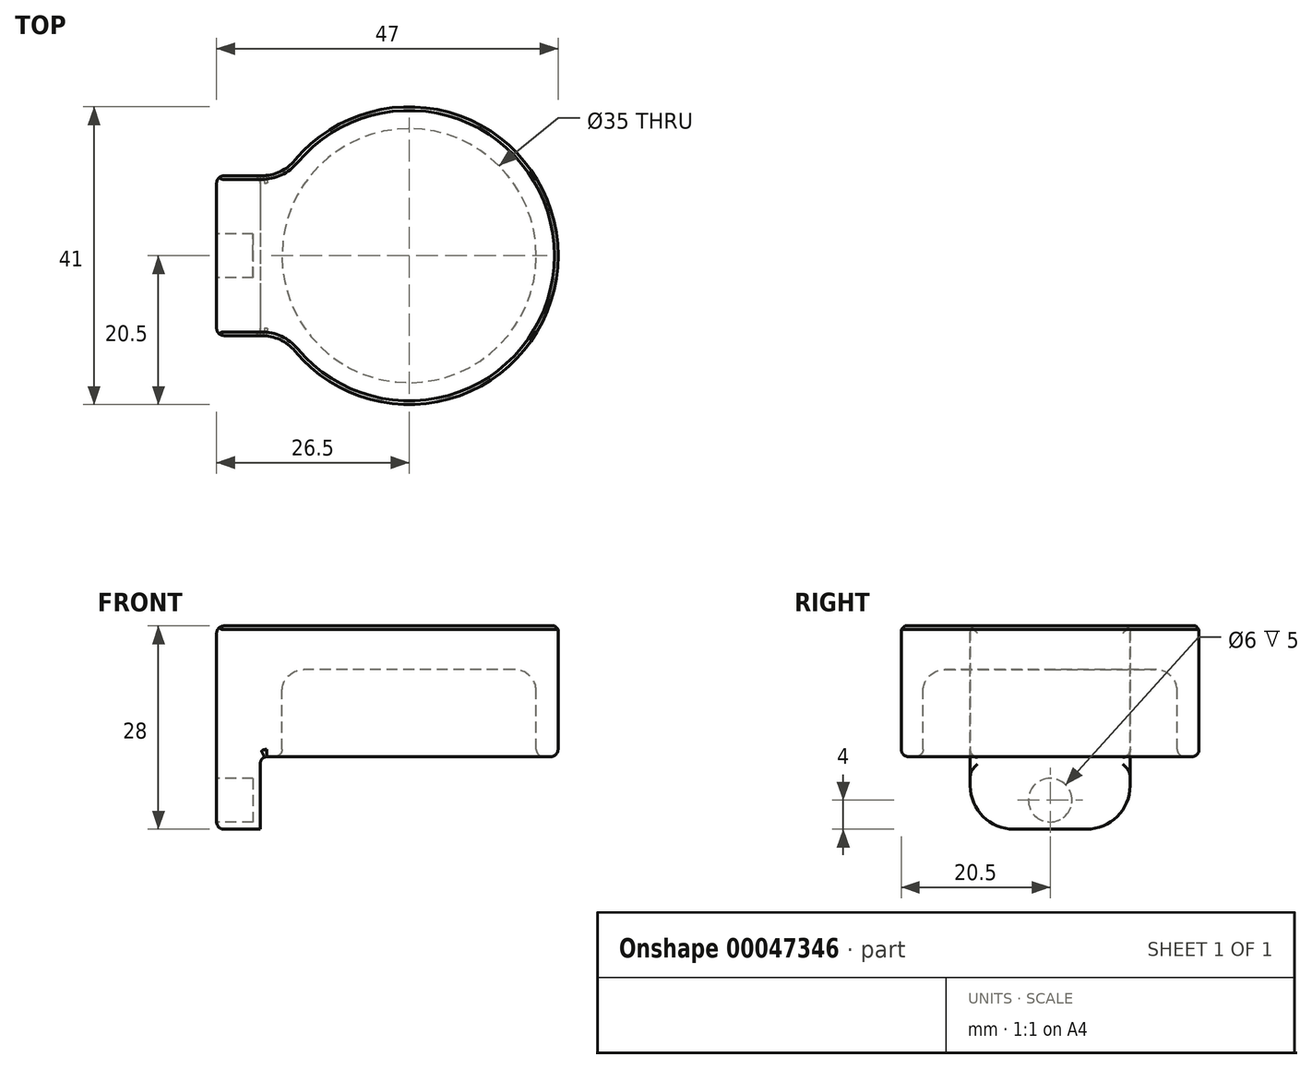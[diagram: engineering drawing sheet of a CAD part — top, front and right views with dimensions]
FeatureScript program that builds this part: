
annotation { "Feature Type Name" : "Feature", "Feature Type Description" : "" }
export const myFeature = defineFeature(function(context is Context, id is Id, definition is map)
    precondition{}
    {
        {
            var Q0;
            Q0=qCreatedBy(makeId("Top.planeOp"),FACE);
            var sketch = newSketch(context, id + "F0", { "sketchPlane" : qUnion([Q0])});
            skCircle(sketch, "E0", {"center": v(0, 0) * mm, "radius": 17.5 * mm});
            skArc(sketch, "E1", {"start": v(-17.3, -11) * mm, "mid": v(20.5, 0) * mm, "end": v(-17.3, 11) * mm});
            skLineSegment(sketch, "E2", {"start": v(-17.3, 11) * mm, "end": v(-26.5, 11) * mm});
            skLineSegment(sketch, "E3", {"start": v(-26.5, 11) * mm, "end": v(-26.5, -11) * mm});
            skLineSegment(sketch, "E4", {"start": v(-26.5, -11) * mm, "end": v(-17.3, -11) * mm});
            skLineSegment(sketch, "E5", {"start": v(0, 0) * mm, "end": v(-26.5, 0) * mm, "construction": true});
            skSolve(sketch);
        }
        {
            var Q0;
            Q0=makeQuery(id+"F0.imprint","IMPRINT",FACE,{"disambiguationData":[TD([[makeQuery(id+"F0.imprint","IMPRINT",EDGE,{"derivedFrom":sQuery(id+"F0.wireOp",EDGE,"E0")}),1.0]])]});
            extrude(context, id + "F1", {"entities" : qUnion([Q0]), "oppositeDirection" : true, "depth" : 6 * mm});
        }
        {
            var Q0;
            Q0=makeQuery(id+"F0.imprint","IMPRINT",FACE,{"disambiguationData":[TD([[makeQuery(id+"F0.imprint","IMPRINT",EDGE,{"derivedFrom":sQuery(id+"F0.wireOp",EDGE,"E0")}),-1.0]])]});
            extrude(context, id + "F2", {"entities" : qUnion([Q0]), "operationType" : NewBodyOperationType.ADD, "oppositeDirection" : true, "depth" : 18 * mm});
        }
        {
            var Q0;
            Q0=makeQuery(id+"F2.opExtrude","CAP_FACE",FACE,{"disambiguationData":[OSD([sQuery(id+"F0.wireOp",EDGE,"E0"),sQuery(id+"F0.wireOp",EDGE,"E1"),sQuery(id+"F0.wireOp",EDGE,"E2"),sQuery(id+"F0.wireOp",EDGE,"E3"),sQuery(id+"F0.wireOp",EDGE,"E4")])],"isStart":false});
            var sketch = newSketch(context, id + "F3", { "sketchPlane" : qUnion([Q0])});
            skLineSegment(sketch, "E6", {"start": v(-20.5, -11) * mm, "end": v(-20.5, 11) * mm});
            skSolve(sketch);
        }
        {
            var Q0;
            Q0=qSketchRegion(id+"F3",true);
            var Q1;
            {var subQ1=sQuery(id+"F3.wireOp",EDGE,"E6");Q1=makeQuery(id+"F3.imprint","IMPRINT",FACE,{"disambiguationData":[TD([[makeQuery(id+"F3.imprint","IMPRINT",EDGE,{"derivedFrom":subQ1}),1.0]])]});}
            extrude(context, id + "F4", {"entities" : qUnion([Q0, Q1]), "operationType" : NewBodyOperationType.ADD, "depth" : 10 * mm});
        }
        {
            var Q0;
            Q0=makeQuery(id+"F2.opExtrude","SWEPT_EDGE",EDGE,{"disambiguationData":[OSD([sQuery(id+"F0.wireOp",EDGE,"E1"),sQuery(id+"F0.wireOp",EDGE,"E2")])]});
            var Q1;
            Q1=makeQuery(id+"F2.opExtrude","SWEPT_EDGE",EDGE,{"disambiguationData":[OSD([sQuery(id+"F0.wireOp",EDGE,"E1"),sQuery(id+"F0.wireOp",EDGE,"E4")])]});
            var Q2;
            Q2=makeQuery(id+"F4.opExtrude","CAP_EDGE",EDGE,{"disambiguationData":[OSD([sQuery(id+"F0.wireOp",EDGE,"E2")])],"isStart":false});
            var Q3;
            Q3=makeQuery(id+"F4.opExtrude","CAP_EDGE",EDGE,{"disambiguationData":[OSD([sQuery(id+"F0.wireOp",EDGE,"E4")])],"isStart":false});
            fillet(context, id + "F5", {"entities" : qUnion([Q0, Q1, Q2, Q3]), "radius" : 6 * mm, "tangentPropagation" : true, "allowEdgeOverflow" : false});
        }
        {
            var Q0;
            Q0=makeQuery(id+"F4.opExtrude","CAP_EDGE",EDGE,{"disambiguationData":[OSD([sQuery(id+"F3.wireOp",EDGE,"E6")])],"isStart":true});
            var Q1;
            Q1=makeQuery(id+"F1.opExtrude","CAP_FACE",FACE,{"disambiguationData":[OSD([sQuery(id+"F0.wireOp",EDGE,"E0")])],"isStart":false});
            fillet(context, id + "F6", {"entities" : qUnion([Q0, Q1]), "radius" : 3 * mm, "tangentPropagation" : true, "allowEdgeOverflow" : false});
        }
        {
            var Q0;
            Q0=makeQuery(id+"F2.opExtrude","CAP_FACE",FACE,{"disambiguationData":[OSD([sQuery(id+"F0.wireOp",EDGE,"E0"),sQuery(id+"F0.wireOp",EDGE,"E1"),sQuery(id+"F0.wireOp",EDGE,"E2"),sQuery(id+"F0.wireOp",EDGE,"E3"),sQuery(id+"F0.wireOp",EDGE,"E4")])],"isStart":false});
            var Q1;
            {var subQ0=sQuery(id+"F0.wireOp",EDGE,"E3");Q1=makeQuery(id+"F4.boolean.opBoolean","MERGE",FACE,{"derivedFrom":[makeQuery(id+"F2.opExtrude","SWEPT_FACE",FACE,{"disambiguationData":[OSD([subQ0])]}),makeQuery(id+"F4.opExtrude","SWEPT_FACE",FACE,{"disambiguationData":[OSD([subQ0])]})]});}
            fillet(context, id + "F7", {"entities" : qUnion([Q0, Q1]), "radius" : 1 * mm, "tangentPropagation" : true, "allowEdgeOverflow" : false});
        }
        {
            var Q0;
            {var subQ0=sQuery(id+"F0.wireOp",EDGE,"E0");Q0=makeQuery(id+"F2.boolean.opBoolean","MERGE",FACE,{"derivedFrom":[makeQuery(id+"F1.opExtrude","CAP_FACE",FACE,{"disambiguationData":[OSD([subQ0])],"isStart":true}),makeQuery(id+"F2.opExtrude","CAP_FACE",FACE,{"disambiguationData":[OSD([subQ0,sQuery(id+"F0.wireOp",EDGE,"E1"),sQuery(id+"F0.wireOp",EDGE,"E2"),sQuery(id+"F0.wireOp",EDGE,"E3"),sQuery(id+"F0.wireOp",EDGE,"E4")])],"isStart":true})]});}
            chamfer(context, id + "F8", {"entities" : qUnion([Q0]), "width" : .5 * mm, "tangentPropagation" : true});
        }
        {
            var Q0;
            {var subQ0=sQuery(id+"F0.wireOp",EDGE,"E3");Q0=makeQuery(id+"F4.boolean.opBoolean","MERGE",FACE,{"derivedFrom":[makeQuery(id+"F2.opExtrude","SWEPT_FACE",FACE,{"disambiguationData":[OSD([subQ0])]}),makeQuery(id+"F4.opExtrude","SWEPT_FACE",FACE,{"disambiguationData":[OSD([subQ0])]})]});}
            var sketch = newSketch(context, id + "F9", { "sketchPlane" : qUnion([Q0])});
            skCircle(sketch, "E7", {"center": v(0, -24) * mm, "radius": 3 * mm});
            skLineSegment(sketch, "E8", {"start": v(0, -27) * mm, "end": v(0, -1) * mm, "construction": true});
            skSolve(sketch);
        }
        {
            var Q0;
            Q0=makeQuery(id+"F9.imprint","IMPRINT",FACE,{"disambiguationData":[TD([[makeQuery(id+"F9.imprint","IMPRINT",EDGE,{"derivedFrom":sQuery(id+"F9.wireOp",EDGE,"E7")}),1.0]])]});
            extrude(context, id + "F10", {"entities" : qUnion([Q0]), "operationType" : NewBodyOperationType.REMOVE, "oppositeDirection" : true, "depth" : 5 * mm});
        }
    });
